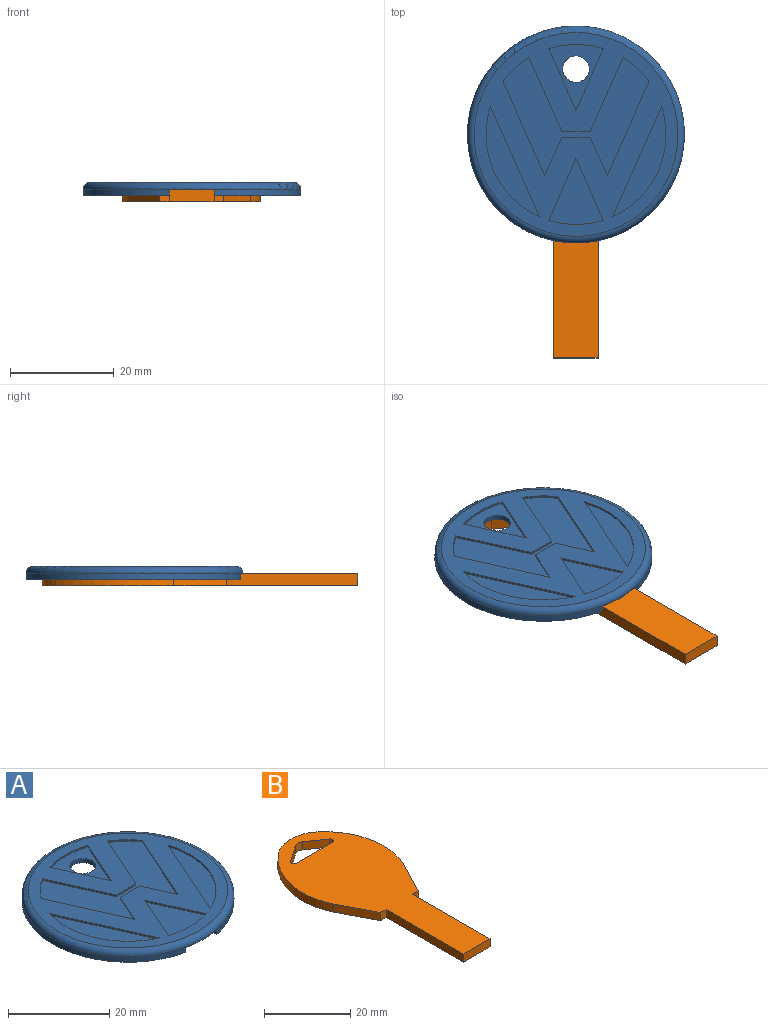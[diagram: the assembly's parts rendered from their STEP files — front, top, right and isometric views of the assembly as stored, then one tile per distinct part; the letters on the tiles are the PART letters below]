
ASSEMBLY  parts=2 mates=1
PART A: 40 faces, bbox 45.4x45.4x2.5 mm
  f0: plane 41.91x41.46mm, normal (0,0,-1), area 612.1mm2, adj f2,f30,f31,f32,f33,f34,f35,f36
  f1: plane 39.37x39.37mm, normal (0,0,1), area 696.2mm2, adj f3,f4,f5,f6,f7,f8,f9,f10
  f2: cylinder r=20.96mm len=41.91mm, axis (0,0,-1), area 157.2mm2, adj f0,f28,f29,f30,f31
  f3: plane 14.3x6.37mm, normal (-0.91,-0.41,0), area 6.3mm2, adj f1,f4,f12,f13
  f4: cylinder r=17.39mm len=5mm, axis (0,0,1), area 2.7mm2, adj f1,f3,f5,f13
  f5: plane 18.11x8.07mm, normal (0.91,0.41,0), area 7.9mm2, adj f1,f4,f6,f13
  f6: plane 7.4x3.3mm, normal (-0.91,0.41,0), area 3.2mm2, adj f1,f5,f7,f13
  f7: plane 5.47x0.4mm, normal (0,1,0), area 2.2mm2, adj f1,f6,f8,f13
  f8: plane 7.4x3.3mm, normal (0.91,0.41,0), area 3.2mm2, adj f1,f7,f9,f13
  f9: plane 18.11x8.07mm, normal (-0.91,0.41,0), area 7.9mm2, adj f1,f8,f10,f13
  f10: cylinder r=17.39mm len=5mm, axis (0,0,1), area 2.7mm2, adj f1,f9,f11,f13
  f11: plane 14.3x6.37mm, normal (0.91,-0.41,0), area 6.3mm2, adj f1,f10,f12,f13
  f12: plane 5.47x0.4mm, normal (0,-1,0), area 2.2mm2, adj f1,f3,f11,f13
  f13: plane 28.19x22.75mm, normal (0,0,1), area 241mm2, adj f3,f4,f5,f6,f7,f8,f9,f10
  f14: cylinder r=17.39mm len=10.58mm, axis (0,0,1), area 4.3mm2, adj f1,f15,f16,f17
  f15: plane 11.88x5.29mm, normal (0.91,0.41,0), area 5.2mm2, adj f1,f14,f16,f17
  f16: plane 11.88x5.29mm, normal (-0.91,0.41,0), area 5.2mm2, adj f1,f14,f15,f17
  f17: plane 12.71x10.58mm, normal (0,0,1), area 48.2mm2, adj f14,f15,f16,f39
  f18: cylinder r=17.39mm len=21.26mm, axis (0,0,1), area 10.2mm2, adj f1,f19,f20
  f19: plane 21.26x9.47mm, normal (-0.91,-0.41,0), area 9.3mm2, adj f1,f18,f20
  f20: plane 21.26x10.32mm, normal (0,0,1), area 71.3mm2, adj f18,f19
  f21: plane 21.26x9.47mm, normal (0.91,-0.41,0), area 9.3mm2, adj f1,f22,f23
  f22: cylinder r=17.39mm len=21.26mm, axis (0,0,1), area 10.2mm2, adj f1,f21,f23
  f23: plane 21.26x10.32mm, normal (0,0,1), area 71.3mm2, adj f21,f22
  f24: plane 11.88x5.29mm, normal (0.91,-0.41,0), area 5.2mm2, adj f1,f25,f26,f27
  f25: cylinder r=17.39mm len=10.58mm, axis (0,0,1), area 4.3mm2, adj f1,f24,f26,f27
  f26: plane 11.88x5.29mm, normal (-0.91,-0.41,0), area 5.2mm2, adj f1,f24,f25,f27
  f27: plane 12.71x10.58mm, normal (0,0,1), area 68.7mm2, adj f24,f25,f26
  f28: torus R=19.69mm, axis (0,0,1), area 256.9mm2, adj f1,f2
  f29: plane 38.74x26.59mm, normal (0,0,-1), area 746.9mm2, adj f2,f30,f31,f32,f33,f34,f35,f36
  f30: plane 2.72x1.14mm, normal (1,0,0), area 3.1mm2, adj f0,f2,f29,f32
  f31: plane 2.72x1.14mm, normal (-1,0,0), area 3.1mm2, adj f0,f2,f29,f38
  f32: plane 1.82x1.14mm, normal (0,1,0), area 2.1mm2, adj f0,f29,f30,f33
  f33: plane 10.16x5.27mm, normal (0.89,0.46,0), area 13.1mm2, adj f0,f29,f32,f34
  f34: cylinder r=19.4mm len=22.86mm, axis (0,0,-1), area 28.6mm2, adj f0,f29,f33,f35
  f35: cylinder r=10.17mm len=13.45mm, axis (0,0,-1), area 16.8mm2, adj f0,f29,f34,f36
  f36: cylinder r=19.4mm len=22.86mm, axis (0,0,-1), area 28.6mm2, adj f0,f29,f35,f37
  f37: plane 10.16x5.27mm, normal (-0.89,0.46,0), area 13.1mm2, adj f0,f29,f36,f38
  f38: plane 1.82x1.14mm, normal (0,1,0), area 2.1mm2, adj f0,f29,f31,f37
  f39: cylinder r=2.56mm len=5.12mm, axis (0,0,1), area 16mm2, adj f17,f29
PART B: 18 faces, bbox 26.6x61x2.3 mm
  f0: plane 25.4x2.29mm, normal (1,0,0), area 58.1mm2, adj f1,f9,f10,f11
  f1: plane 2.29x1.82mm, normal (0,-1,0), area 4.2mm2, adj f0,f2,f10,f11
  f2: plane 10.16x5.27mm, normal (0.89,-0.46,0), area 26.2mm2, adj f1,f3,f10,f11
  f3: cylinder r=19.4mm len=22.86mm, axis (0,0,-1), area 57.2mm2, adj f2,f4,f10,f11
  f4: cylinder r=10.17mm len=13.45mm, axis (0,0,-1), area 33.6mm2, adj f3,f5,f10,f11
  f5: cylinder r=19.4mm len=22.86mm, axis (0,0,-1), area 57.2mm2, adj f4,f6,f10,f11
  f6: plane 10.16x5.27mm, normal (-0.89,-0.46,0), area 26.2mm2, adj f5,f7,f10,f11
  f7: plane 2.29x1.82mm, normal (0,-1,0), area 4.2mm2, adj f6,f8,f10,f11
  f8: plane 25.4x2.29mm, normal (-1,0,0), area 58.1mm2, adj f7,f9,f10,f11
  f9: plane 8.69x2.29mm, normal (0,-1,0), area 19.9mm2, adj f0,f8,f10,f11
  f10: plane 60.96x26.59mm, normal (0,0,1), area 915.4mm2, adj f0,f1,f2,f3,f4,f5,f6,f7
  f11: plane 60.96x26.59mm, normal (0,0,-1), area 915.4mm2, adj f0,f1,f2,f3,f4,f5,f6,f7
  f12: cylinder r=2.03mm len=2.31mm, axis (0,0,1), area 5.6mm2, adj f10,f11,f13,f17
  f13: plane 5.25x3.63mm, normal (0.57,-0.82,0), area 14.6mm2, adj f10,f11,f12,f14
  f14: cylinder r=0.76mm len=2.29mm, axis (0,0,1), area 4.4mm2, adj f10,f11,f13,f15
  f15: plane 11.94x2.29mm, normal (0,1,0), area 27.3mm2, adj f10,f11,f14,f16
  f16: cylinder r=0.76mm len=2.29mm, axis (0,0,1), area 4.4mm2, adj f10,f11,f15,f17
  f17: plane 5.25x3.63mm, normal (-0.57,-0.82,0), area 14.6mm2, adj f10,f11,f12,f16
PLACE A t=(0,0,-15.96)mm
PLACE B rot(axis=(0,1,0),180deg) t=(-0.08,-30.47,-15.96)mm
MATE planar B.f11 <-> A.f29  axis (0,0,1) through (-0.08,-8.07,-14.82)mm
